# Revit family: Faucet-Sloan-Optima-EFT-410_EBF-415
name_source: partatom
category: Plumbing Fixtures
revit_build: Autodesk Revit 2016 (Build: 20150714_1515(x64)
units: mm (PartAtom-declared; Revit-internal decimal feet)

## family parameters
Always vertical = No
Cut with Voids When Loaded = No
OmniClass Number = 23.45.55.14
OmniClass Title = Single Faucets
Part Type = Normal
Room Calculation Point = No
Round Connector Dimension = Use Radius
Shared = Yes
Work Plane-Based = Yes

## types (2) — shared parameters
0.35 GPM/1.3 Lpm = No
0.5 GPM/1.9 Lpm = Yes
Assembly Code = D2020300
CW Connection = Yes
CWFU = 1.5
Cold Water Connection Radius = 3/16"
Countertop Thickness = 1 1/2"
Default Elevation = 0"
Finish = Cast Brass-Sloan-Chrome Plated
Flow Rates = 0.5 GPM/1.9 Lpm
Global Connection Radius = 3/16"
HW Connection = Yes
HWFU = 1.5
Height = 4 1/2"
Hot Water Connection Radius = 3/16"
Installation Type = Deck Mounted
Length = 5 1/2"
Manufacturer = SLOAN
Material = Cast Brass-Sloan-Chrome Plated
Operation = Sensor Activated
Revised Date = 7/32/20
URL = https://www.sloan.com
Vent Connection = No
Waste Connection = No
Width = 2"
zero-valued in all types: WFU

## per-type parameters (varying)
| type | Description | Model | Warranty Documentation Link |
| EFT-410 | Optima Deck Mount, hardwired, Sensor Activated Electronic Hand Washing Faucet for pre-tempered or hot and cold water operation. | EFT-420 | https://www.sloan.com |
| EBF-415 | Optima Deck Mount, battery, Sensor Activated Electronic Hand Washing Faucet for pre-tempered or hot and cold water operation. | EBF-425 |  |

## geometry (parser evidence)
native form markers: Sweep x2
no freeform markers — native parametric forms only
